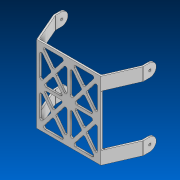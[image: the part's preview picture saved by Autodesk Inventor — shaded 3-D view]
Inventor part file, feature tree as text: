
AUTODESK INVENTOR PART (.ipt)
format: ipt  version: 2022 (Build 260153000, 153)  size: 355,328 bytes
history: native  units: in
note: dims shown in document units (in); Inventor stores cm internally (conversion verified against a paired STEP export)
features: fillet x3, sketch x3, extrude x2, hole x1, mirror x1, projected_geometry x1
ambient origin geometry x8: Origin, YZ Plane, XZ Plane, XY Plane, X Axis, Y Axis, Z Axis, Center Point
bodies: Solid1 (feature_tree)
feature tree (11):
  extrude  "Extrusion1"  Depth=6.0in
  fillet  "Fillet1"  Radius=0.125in
  extrude  "Extrusion2"  Depth=0.125in
  fillet  "Fillet2"  Radius=0.125in
  fillet  "Fillet3"  Radius=0.125in
  hole  "Hole1"  [1 undecoded]
  mirror  "Mirror1"
  sketch  "Sketch1"  dims[d0=5.0in d1=6.0in d2=0.125in d3=0.0in]
  sketch  "Sketch2"  dims[d4=0.25in d5=0.125in d6=0.125in d7=0.125in]
  projected_geometry  "Projected Loop1"
  sketch  "Sketch3"  dims[d8=0.125in d9=0.125in d10=0.125in d11=0.125in d12=1.0in d13=2.3125in d14=0.125in d15=7.0in d16=0.125in d17=0.125in d18=1.0in d19=0.0in d20=0.15in d21=0.05in d22=0.5in d23=0.18in d24=0.75in d25=0.375in d26=0.25in d27=0.5635in d28=1.0in d29=0.8108in]
note: 1 required parameter value undecoded (feature->parameter linkage not recoverable at this tier; creation-order binding heuristic only, values carry confidence <= 0.55)
